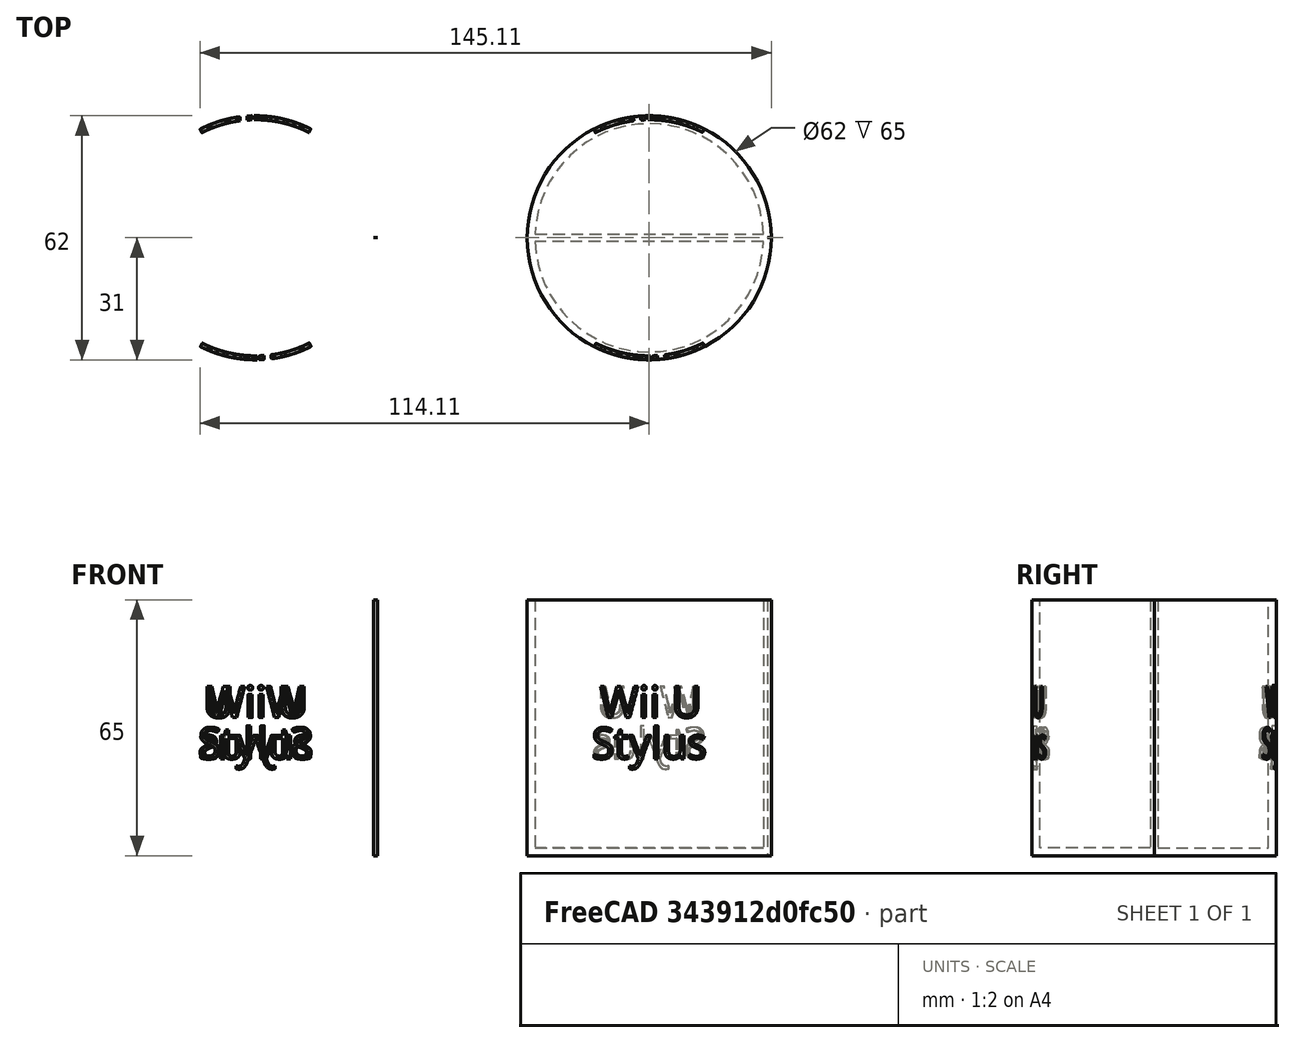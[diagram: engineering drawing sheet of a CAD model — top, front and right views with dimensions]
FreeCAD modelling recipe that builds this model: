
FCSTD DOCUMENT  (FreeCAD 0.21R33668 +7 (Git))
Label: Stylus Cups
License: All rights reserved
LicenseURL: http://en.wikipedia.org/wiki/All_rights_reserved
objects: Part::Part2DObjectPython×4, Sketcher::SketchObject×3, PartDesign::Body×2, Part::FeaturePython×2, PartDesign::Pad×1, PartDesign::Pocket×1, App::DocumentObjectGroup×1, PartDesign::FeatureBase×1, Part::Cut×1
note: 17 computed .brp shape members not serialized (recipe doc carries the construction recipe); baked Part::Feature solids carry a one-line shape summary decoded from their .brp

FEATURE [Sketcher::SketchObject] Sketch
  FullyConstrained = true
  MapMode = 5
  Support = -> [XY_Plane]
  sketch-geometry (1):
    g0: Circle CenterX=0 CenterY=0 CenterZ=0 NormalX=0 NormalY=0 NormalZ=1 AngleXU=0 Radius=31
  constraints (2):
    c: Coincident(g0,g-1)
    c: Diameter(g0) = 62
FEATURE [PartDesign::Pad] Pad
  Direction = (0,0,1)
  Length = 65
  Length2 = 10
  Profile = -> Sketch
  ReferenceAxis = -> Sketch [N_Axis]
  Type = 0
FEATURE [Sketcher::SketchObject] Sketch001
  ExternalGeometry = -> [Pad]
  FullyConstrained = true
  MapMode = 5
  Placement = pos=(0,0,65) rot=(0,0,1;0rad)
  Support = -> [Pad]
  sketch-geometry (6):
    g0: Circle CenterX=0 CenterY=0 CenterZ=0 NormalX=0 NormalY=0 NormalZ=1 AngleXU=0 Radius=29
    g1: LineSegment StartX=-28.9828 StartY=1 StartZ=0 EndX=28.9828 EndY=1 EndZ=0
    g2: LineSegment StartX=28.9828 StartY=-1 StartZ=0 EndX=-28.9828 EndY=-1 EndZ=0
    g3: LineSegment StartX=0 StartY=1 StartZ=0 EndX=0 EndY=-1 EndZ=0
    g4: ArcOfCircle CenterX=-1.5e-15 CenterY=-5.12e-14 CenterZ=0 NormalX=0 NormalY=0 NormalZ=1 AngleXU=0 Radius=29 StartAngle=0.0344896 EndAngle=3.1071
    g5: ArcOfCircle CenterX=-1.5e-15 CenterY=5.44e-14 CenterZ=0 NormalX=0 NormalY=0 NormalZ=1 AngleXU=0 Radius=29 StartAngle=3.17608 EndAngle=6.2487
  constraints (19):
    c: Coincident(g0,g-3)
    c: PointOnObject(g1,g0)
    c: PointOnObject(g1,g0)
    c: Horizontal(g1)
    c: PointOnObject(g2,g0)
    c: PointOnObject(g2,g0)
    c: Horizontal(g2)
    c: PointOnObject(g3,g1)
    c: PointOnObject(g3,g2)
    c: Vertical(g3)
    c: Symmetric(g3,g3,g0)
    c: Distance(g3) = 2
    c: Coincident(g4,g1)
    c: Coincident(g4,g1)
    c: Coincident(g5,g2)
    c: Coincident(g5,g2)
    c: Equal(g4,g0)
    c: Equal(g5,g0)
    c: Diameter(g0) = 58
FEATURE [PartDesign::Pocket] Pocket
  BaseFeature = -> Pad
  Direction = (0,0,-1)
  Length = 63
  Length2 = 5
  Profile = -> Sketch001
  ReferenceAxis = -> Sketch001 [N_Axis]
  Refine = true
  Type = 0
FEATURE [PartDesign::Body] Body  label="Blank Cup"
  Group = -> [Sketch,Pad,Sketch001,Pocket]
  Origin = -> Origin
  Tip = -> Pocket
FEATURE [Sketcher::SketchObject] Mapped_Sketch
  FullyConstrained = true
  Support = -> [Pocket]
  sketch-geometry (5):
    g0: LineSegment StartX=0 StartY=-65 StartZ=0 EndX=194.779 EndY=-65 EndZ=0
    g1: LineSegment StartX=194.779 StartY=-65 StartZ=0 EndX=194.779 EndY=0 EndZ=0
    g2: LineSegment StartX=194.779 StartY=0 StartZ=0 EndX=0 EndY=0 EndZ=0
    g3: LineSegment StartX=0 StartY=0 StartZ=0 EndX=0 EndY=-65 EndZ=0
    g4: LineSegment StartX=97.3894 StartY=0 StartZ=0 EndX=97.3894 EndY=-65 EndZ=0
  constraints (15):
    c: Coincident(g0,g1)
    c: Coincident(g1,g2)
    c: Coincident(g2,g3)
    c: Coincident(g3,g0)
    c: Horizontal(g0)
    c: Horizontal(g2)
    c: Vertical(g1)
    c: Vertical(g3)
    c: DistanceX(g2,g2) = 194.779
    c: DistanceY(g1,g1) = 65
    c: DistanceX(g0,g-1) = 0
    c: DistanceY(g0,g-1) = 65
    c: PointOnObject(g4,g2)
    c: Vertical(g4)
    c: Symmetric(g0,g0,g4)
FEATURE [Part::Part2DObjectPython] ShapeString  label="Stylus Front"  # Draft 2D object (typed FeaturePython)
  FontFile = F:/16 Bit Git Repro/16 Bit Store/Font/OpenSans-Regular.ttf
  MakeFace = true
  Placement = pos=(130.99,-40.36,0) rot=(0,0,-1;0rad)
  Size = 10
  String = Stylus
  Tracking = 0
FEATURE [Part::Part2DObjectPython] ShapeString001  label="System Front"  # Draft 2D object (typed FeaturePython)
  FontFile = F:/16 Bit Git Repro/16 Bit Store/Font/OpenSans-Regular.ttf
  MakeFace = true
  Placement = pos=(133.2,-29.86,0) rot=(0,0,1;0rad)
  Size = 10
  String = Wii U
  Tracking = 0
FEATURE [Part::Part2DObjectPython] ShapeString002  label="Stylus Back"  # Draft 2D object (typed FeaturePython)
  FontFile = F:/16 Bit Git Repro/16 Bit Store/Font/OpenSans-Regular.ttf
  MakeFace = true
  Placement = pos=(33.6,-40.36,0) rot=(0,0,-0.894427;0rad)
  Size = 10
  String = Stylus
  Tracking = 0
FEATURE [Part::Part2DObjectPython] ShapeString003  label="System Back"  # Draft 2D object (typed FeaturePython)
  FontFile = F:/16 Bit Git Repro/16 Bit Store/Font/OpenSans-Regular.ttf
  MakeFace = true
  Placement = pos=(35.81,-29.86,0) rot=(0,0,1;0rad)
  Size = 10
  String = Wii U
  Tracking = 0
FEATURE [Part::FeaturePython] Sketch_On_Surface  # WARN: FeaturePython — macro-defined, semantics opaque (R4)
  ConstructionBounds = true
  ExtraObjects = -> [ShapeString,ShapeString001,ShapeString002,ShapeString003]
  FillExtrusion = true
  FillFaces = true
  ReverseU = false
  ReverseV = true
  Sketch = -> Mapped_Sketch
  SwapUV = false
  Thickness = -1
FEATURE [App::DocumentObjectGroup] Group  label="Base Text"
  Group = -> [Sketch_On_Surface,ShapeString,ShapeString001,ShapeString002,ShapeString003]
FEATURE [Part::FeaturePython] Sketch_On_Surface002  # WARN: FeaturePython — macro-defined, semantics opaque (R4)
  ConstructionBounds = true
  ExtraObjects = -> [ShapeString,ShapeString001,ShapeString002,ShapeString003]
  FillExtrusion = true
  FillFaces = true
  ReverseU = false
  ReverseV = true
  Sketch = -> Mapped_Sketch
  SwapUV = false
  Thickness = -1
FEATURE [PartDesign::FeatureBase] Clone001
  BaseFeature = -> Body
FEATURE [PartDesign::Body] Body002
  Group = -> [Clone001]
  Origin = -> Origin002
  Tip = -> Clone001
FEATURE [Part::Cut] Cut001  label="Text Cup"
  Base = -> Body002
  Placement = pos=(100,0,0) rot=(0,0,1;0rad)
  Tool = -> Sketch_On_Surface002
